# Revit family: Valve-Safety_Shutoff-Cla_Val-50_33-Grooved--
name_source: partatom
category: Pipe Accessories
units: mm (PartAtom-declared; Revit-internal decimal feet)

## family parameters
Always vertical = Yes
Cut with Voids When Loaded = No
Part Type = Valve - Breaks Into
Round Connector Dimension = Use Diameter
Shared = No
Work Plane-Based = No

## types (1)
- ERROR_LOAD TYPE CATALOG
    Assembly Code = D2090
    Body Material = Metal - CLA-VAL - Ductile Iron - Blue
    Connection Axis to Valve Bottom = 2.000 in
    Connection Axis to Valve Top = 4.750 in
    Connection End Length = 0.943 in
    Connection Radius = 1"
    Connection Size = 2"
    Connection Type = Grooved
    Connection to Connection = 8.500 in
    Control Tube Line Size Diameter = 0"
    Control Tube Line Size Radius = 0"
    Cover Port Center Offset = 1.014 in
    Cover Upper Flange Diameter = 5.620 in
    Cv Coefficient = 32
    Default Elevation = 0.000 in
    Description = Safety Shutoff Valve
    ENGworks URL = http://www.ENGworksGlobal.com
    Flow Configuration = In/Out
    Grooved Diameter = 1.775 in
    Grooved End Length = 0.630 in
    Grooved Length = 0.313 in
    Grooved Outside Diameter = 1.900 in
    Grooved Outside Radius = 0.950 in
    Grooved Radius = 0.888 in
    K Coefficient = 5.9
    K Coefficient Table = Globe Valve Flanged
    Loss Method = K Coefficient
    Manufacturer = Cla-Val
    Maximum Flow Rate = 125 GPM
    Maximum Flow Rate Value = 125
    Maximum Operating Temperature = 180 °F
    Maximum Working Pressure = 400.00 psi
    Minimum Flow Rate = 0 GPM
    Minimum Flow Rate Value = 0
    Minimum Operating Temperature = -40 °F
    Model = 50-33
    Overall Length = 8.500 in
    Pilot Line Angle Offset = 2.499 in
    Pilot Line Height Offset = 0.713 in
    Pilot System Offset = 3.372 in
    Pipe Plug Circumscribe Length = 0.250 in
    Product Page URL = https://www.cla-val.com
    Series = Safety Shutoff Valve
    Side Port Outside Diameter = 0.375 in
    Side Ports Offset from Flange = 1.771 in
    Standards = ASTM A536, B16.42
    Tick Size = 4.907 in
    URL = https://www.cla-val.com
    Unit Weight = 15.00 lb
    Unit Weight Value = 15
    Valve Body Bottom Radius = 1.283 in
    Version = 1
    X Pilot System Offset = 11.000 in
    Y Pilot System Offset = 9.000 in
    Z Pilot System Offset = 9.000 in

## geometry (parser evidence)
native form markers: Sweep x10
no freeform markers — native parametric forms only
